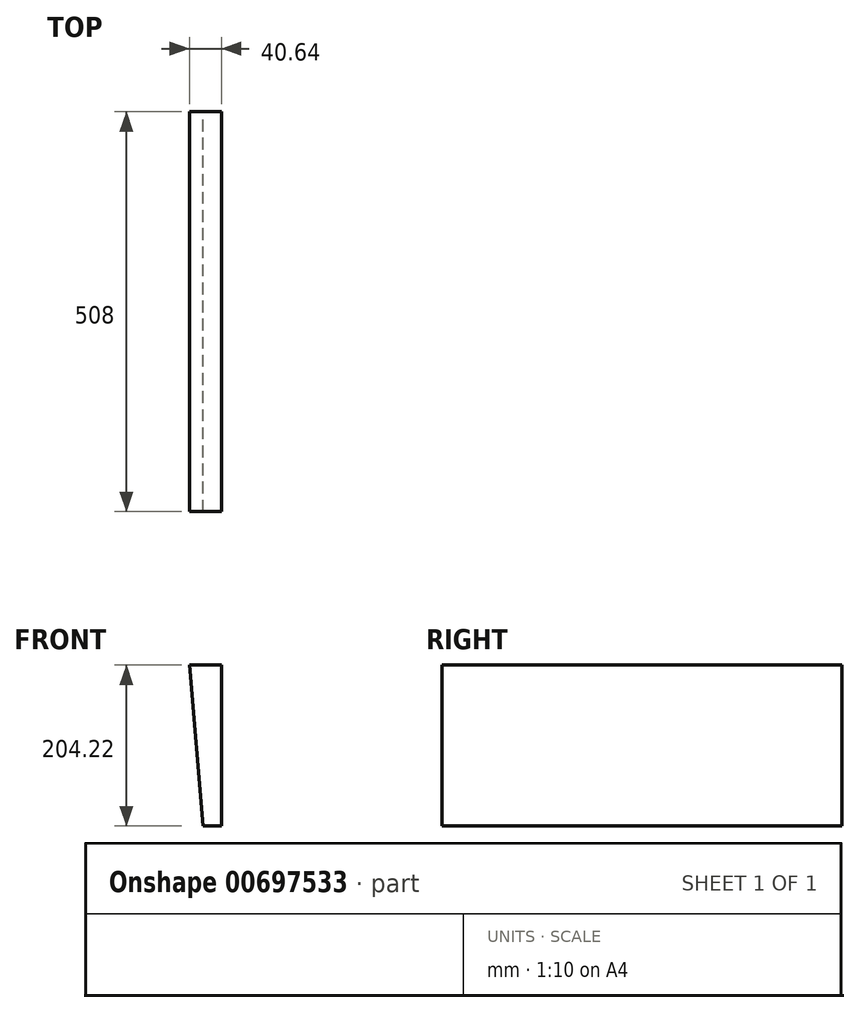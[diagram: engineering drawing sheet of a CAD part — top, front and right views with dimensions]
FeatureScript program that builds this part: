
annotation { "Feature Type Name" : "Feature", "Feature Type Description" : "" }
export const myFeature = defineFeature(function(context is Context, id is Id, definition is map)
    precondition{}
    {
        {
            var Q0;
            Q0=qCreatedBy(makeId("Front.planeOp"),FACE);
            var sketch = newSketch(context, id + "F0", { "sketchPlane" : qUnion([Q0])});
            skLineSegment(sketch, "E0", {"start": v(0, 0) * mm, "end": v(-22.86, 0) * mm});
            skLineSegment(sketch, "E1", {"start": v(-22.86, 0) * mm, "end": v(-40.64, 204.22) * mm});
            skLineSegment(sketch, "E2", {"start": v(-40.64, 204.22) * mm, "end": v(0, 204.22) * mm});
            skLineSegment(sketch, "E3", {"start": v(0, 204.22) * mm, "end": v(0, 0) * mm});
            skSolve(sketch);
        }
        {
            var Q0;
            Q0 = qSketchRegion(id + "F0", true);
            extrude(context, id + "F1", {"entities" : qUnion([Q0]), "depth" : 508 * mm, "offsetDistance" : 25.4 * mm});
        }
    });
